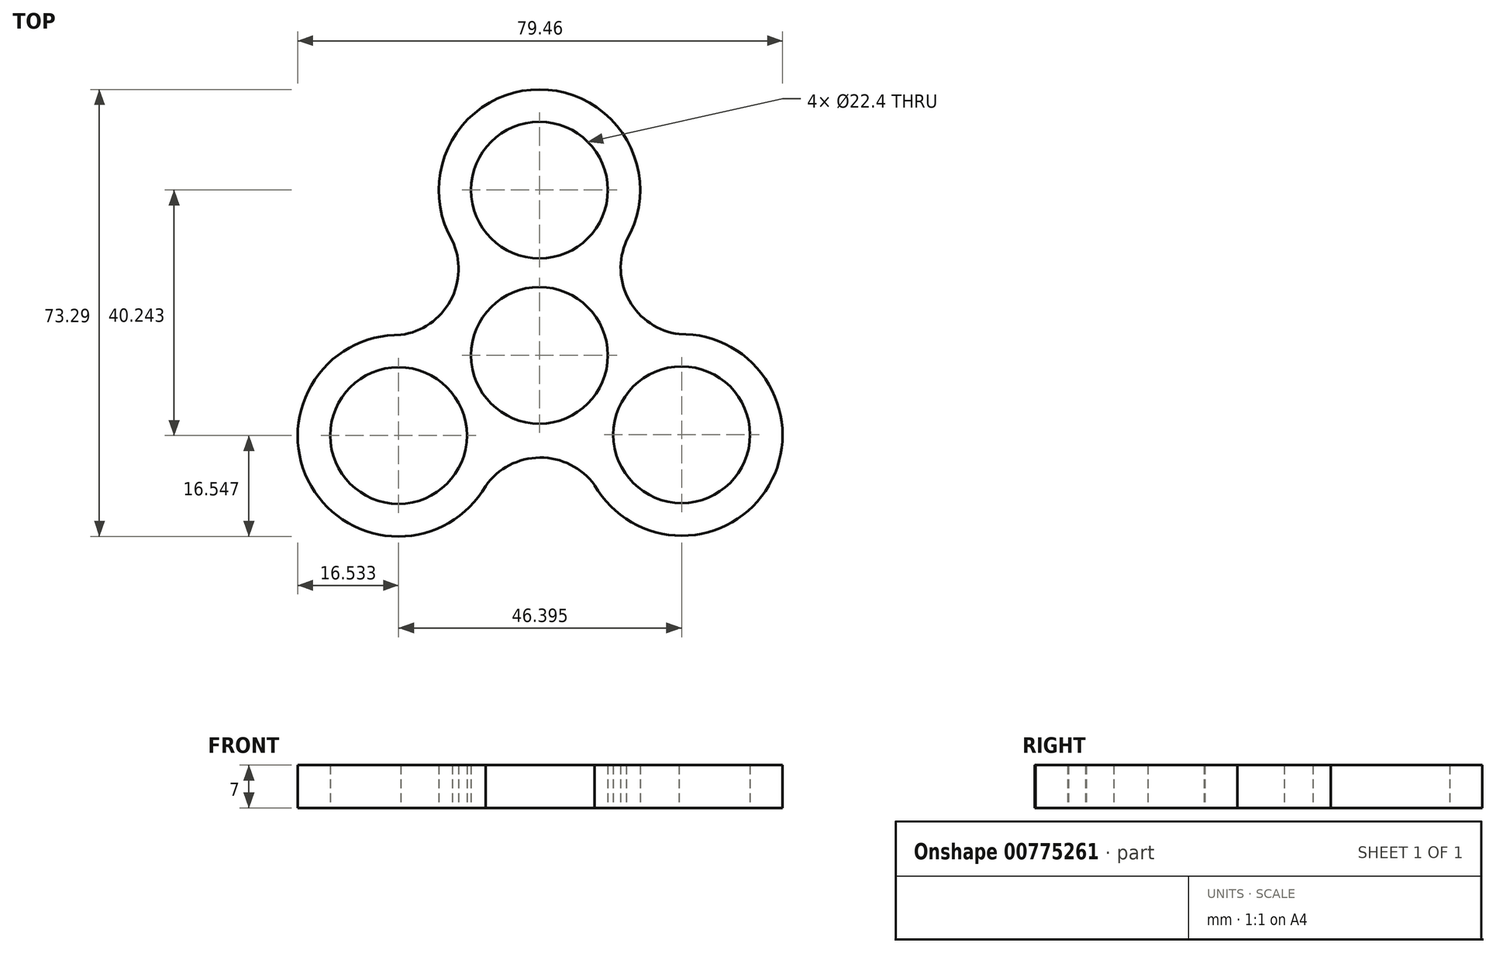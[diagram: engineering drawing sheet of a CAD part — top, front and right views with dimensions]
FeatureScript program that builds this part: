
annotation { "Feature Type Name" : "Feature", "Feature Type Description" : "" }
export const myFeature = defineFeature(function(context is Context, id is Id, definition is map)
    precondition{}
    {
        {
            var Q0;
            Q0=qCreatedBy(makeId("Top.planeOp"),FACE);
            var sketch = newSketch(context, id + "F0", { "sketchPlane" : qUnion([Q0])});
            skCircle(sketch, "E0", {"center": v(0, 0) * mm, "radius": 11.2 * mm});
            skCircle(sketch, "E1", {"center": v(0, 27.1) * mm, "radius": 11.2 * mm});
            skArc(sketch, "E2", {"start": v(14.27, 18.82) * mm, "mid": v(0, 43.6) * mm, "end": v(-14.27, 18.83) * mm});
            skCircle(sketch, "E3.1.0", {"center": v(-23.09, -13.14) * mm, "radius": 11.2 * mm});
            skArc(sketch, "E3.1.1", {"start": v(-22.7, 3.35) * mm, "mid": v(-37.48, -21.21) * mm, "end": v(-8.81, -21.42) * mm});
            skCircle(sketch, "E3.2.0", {"center": v(23.3, -13.01) * mm, "radius": 11.2 * mm});
            skArc(sketch, "E3.2.1", {"start": v(9.03, -21.28) * mm, "mid": v(37.7, -21.07) * mm, "end": v(22.89, 3.48) * mm});
            skPoint(sketch, "E3.center", {"position": v(0.07, 0.31) * mm});
            skArc(sketch, "E4.2.0", {"start": v(-23.08, 3.3) * mm, "mid": v(-37.4, -21.44) * mm, "end": v(-8.81, -21.42) * mm});
            skArc(sketch, "E4.4.0", {"start": v(9.03, -21.28) * mm, "mid": v(37.63, -21.32) * mm, "end": v(23.3, 3.43) * mm});
            skPoint(sketch, "E4.center", {"position": v(0.07, 0.28) * mm});
            skArc(sketch, "E5", {"start": v(14.27, 18.82) * mm, "mid": v(14.83, 8.8) * mm, "end": v(23.3, 3.43) * mm});
            skArc(sketch, "E6.1.0", {"start": v(-22.7, 3.35) * mm, "mid": v(-14.59, 8.97) * mm, "end": v(-14.27, 18.83) * mm});
            skArc(sketch, "E6.2.0", {"start": v(9.03, -21.28) * mm, "mid": v(0.07, -16.76) * mm, "end": v(-8.81, -21.42) * mm});
            skSolve(sketch);
        }
        {
            var Q0;
            Q0=qSketchRegion(id+"F0",true);
            extrude(context, id + "F1", {"entities" : qUnion([Q0]), "depth" : 7 * mm, "offsetDistance" : 25 * mm});
        }
    });
